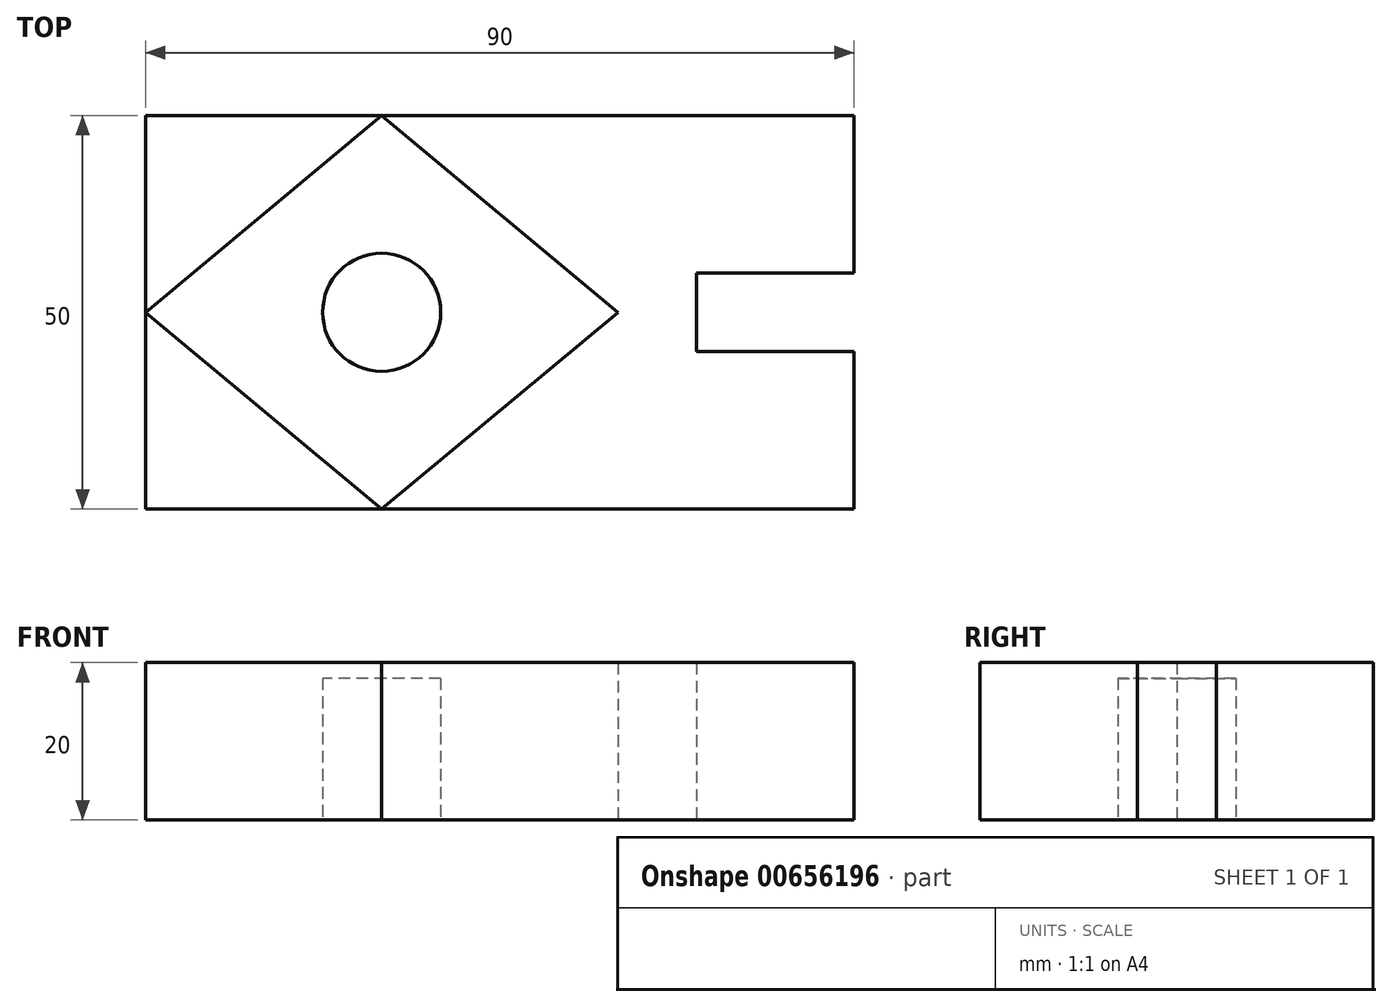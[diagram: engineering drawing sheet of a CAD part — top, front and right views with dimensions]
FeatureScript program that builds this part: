
annotation { "Feature Type Name" : "Feature", "Feature Type Description" : "" }
export const myFeature = defineFeature(function(context is Context, id is Id, definition is map)
    precondition{}
    {
        {
            var Q0;
            Q0=qCreatedBy(makeId("Top.planeOp"),FACE);
            var sketch = newSketch(context, id + "F0", { "sketchPlane" : qUnion([Q0])});
            skLineSegment(sketch, "E0.bottom", {"start": v(-30, -25) * mm, "end": v(30, -25) * mm});
            skLineSegment(sketch, "E0.top", {"start": v(-30, 25) * mm, "end": v(30, 25) * mm});
            skLineSegment(sketch, "E0.left", {"start": v(-30, -25) * mm, "end": v(-30, 25) * mm});
            skLineSegment(sketch, "E0.right", {"start": v(30, -25) * mm, "end": v(30, 25) * mm});
            skPoint(sketch, "E0.middle", {"position": v(0, 0) * mm});
            skLineSegment(sketch, "E1.bottom", {"start": v(-60, -25) * mm, "end": v(60, -25) * mm});
            skLineSegment(sketch, "E1.top", {"start": v(-60, 25) * mm, "end": v(60, 25) * mm});
            skLineSegment(sketch, "E1.left", {"start": v(-60, -25) * mm, "end": v(-60, -5) * mm});
            skLineSegment(sketch, "E1.right", {"start": v(60, -25) * mm, "end": v(60, -5) * mm});
            skLineSegment(sketch, "E2", {"start": v(60, 25) * mm, "end": v(60, 11.2) * mm});
            skLineSegment(sketch, "E3", {"start": v(60, 25) * mm, "end": v(60, 5) * mm});
            skLineSegment(sketch, "E4.trimOffspring", {"start": v(60, 5) * mm, "end": v(60, 25) * mm});
            skLineSegment(sketch, "E5", {"start": v(60, 5) * mm, "end": v(40, 5) * mm});
            skLineSegment(sketch, "E6", {"start": v(60, -5) * mm, "end": v(40, -5) * mm});
            skLineSegment(sketch, "E7", {"start": v(-60, 25) * mm, "end": v(-60, 5) * mm});
            skLineSegment(sketch, "E8", {"start": v(-60, -5) * mm, "end": v(-60, -25) * mm});
            skLineSegment(sketch, "E9.trimOffspring", {"start": v(-60, 5) * mm, "end": v(-60, 25) * mm});
            skLineSegment(sketch, "E10", {"start": v(-60, 5) * mm, "end": v(-40, 5) * mm});
            skLineSegment(sketch, "E11", {"start": v(-60, -5) * mm, "end": v(-40, -5) * mm});
            skLineSegment(sketch, "E12", {"start": v(-40, 5) * mm, "end": v(-40, -5) * mm});
            skLineSegment(sketch, "E13", {"start": v(40, 5) * mm, "end": v(40, -5) * mm});
            skLineSegment(sketch, "E14", {"start": v(0, 25) * mm, "end": v(-30, 0) * mm});
            skLineSegment(sketch, "E15", {"start": v(0, 25) * mm, "end": v(30, 0) * mm});
            skLineSegment(sketch, "E16", {"start": v(30, 0) * mm, "end": v(0, -25) * mm});
            skLineSegment(sketch, "E17", {"start": v(-30, 0) * mm, "end": v(0, -25) * mm});
            skCircle(sketch, "E18", {"center": v(0, 0) * mm, "radius": 9 * mm});
            skSolve(sketch);
        }
        {
            var Q0;
            {var subQ9=sQuery(id+"F0.wireOp",EDGE,"E1.right");Q0=makeQuery(id+"F0.imprint","IMPRINT",FACE,{"disambiguationData":[TD([[makeQuery(id+"F0.imprint","IMPRINT",EDGE,{"derivedFrom":subQ9}),1.0]])]});}
            var Q1;
            {var subQ3=sQuery(id+"F0.wireOp",EDGE,"E16");Q1=makeQuery(id+"F0.imprint","IMPRINT",FACE,{"disambiguationData":[TD([[makeQuery(id+"F0.imprint","IMPRINT",EDGE,{"derivedFrom":subQ3}),1.0]])]});}
            var Q2;
            {var subQ3=sQuery(id+"F0.wireOp",EDGE,"E17");Q2=makeQuery(id+"F0.imprint","IMPRINT",FACE,{"disambiguationData":[TD([[makeQuery(id+"F0.imprint","IMPRINT",EDGE,{"derivedFrom":subQ3}),-1.0]])]});}
            var Q3;
            {var subQ3=sQuery(id+"F0.wireOp",EDGE,"E14");Q3=makeQuery(id+"F0.imprint","IMPRINT",FACE,{"disambiguationData":[TD([[makeQuery(id+"F0.imprint","IMPRINT",EDGE,{"derivedFrom":subQ3}),-1.0]])]});}
            var Q4;
            {var subQ3=sQuery(id+"F0.wireOp",EDGE,"E15");Q4=makeQuery(id+"F0.imprint","IMPRINT",FACE,{"disambiguationData":[TD([[makeQuery(id+"F0.imprint","IMPRINT",EDGE,{"derivedFrom":subQ3}),1.0]])]});}
            var Q5;
            {var subQ6=sQuery(id+"F0.wireOp",EDGE,"E8");Q5=makeQuery(id+"F0.imprint","IMPRINT",FACE,{"disambiguationData":[TD([[makeQuery(id+"F0.imprint","IMPRINT",EDGE,{"derivedFrom":subQ6}),1.0]])]});}
            extrude(context, id + "F1", {"entities" : qUnion([Q0, Q1, Q2, Q3, Q4, Q5]), "depth" : 20 * mm, "offsetDistance" : 25 * mm});
        }
        {
            var Q0;
            Q0=qCreatedBy(makeId("Top.planeOp"),FACE);
            var sketch = newSketch(context, id + "F2", { "sketchPlane" : qUnion([Q0])});
            skCircle(sketch, "E19", {"center": v(0, 0) * mm, "radius": 7.5 * mm});
            skSolve(sketch);
        }
        {
            var Q0;
            Q0=makeQuery(id+"F2.imprint","IMPRINT",FACE,{"disambiguationData":[TD([[makeQuery(id+"F2.imprint","IMPRINT",EDGE,{"derivedFrom":sQuery(id+"F2.wireOp",EDGE,"E19")}),1.0]])]});
            extrude(context, id + "F3", {"entities" : qUnion([Q0]), "depth" : 18 * mm, "offsetDistance" : 25 * mm});
        }
    });
